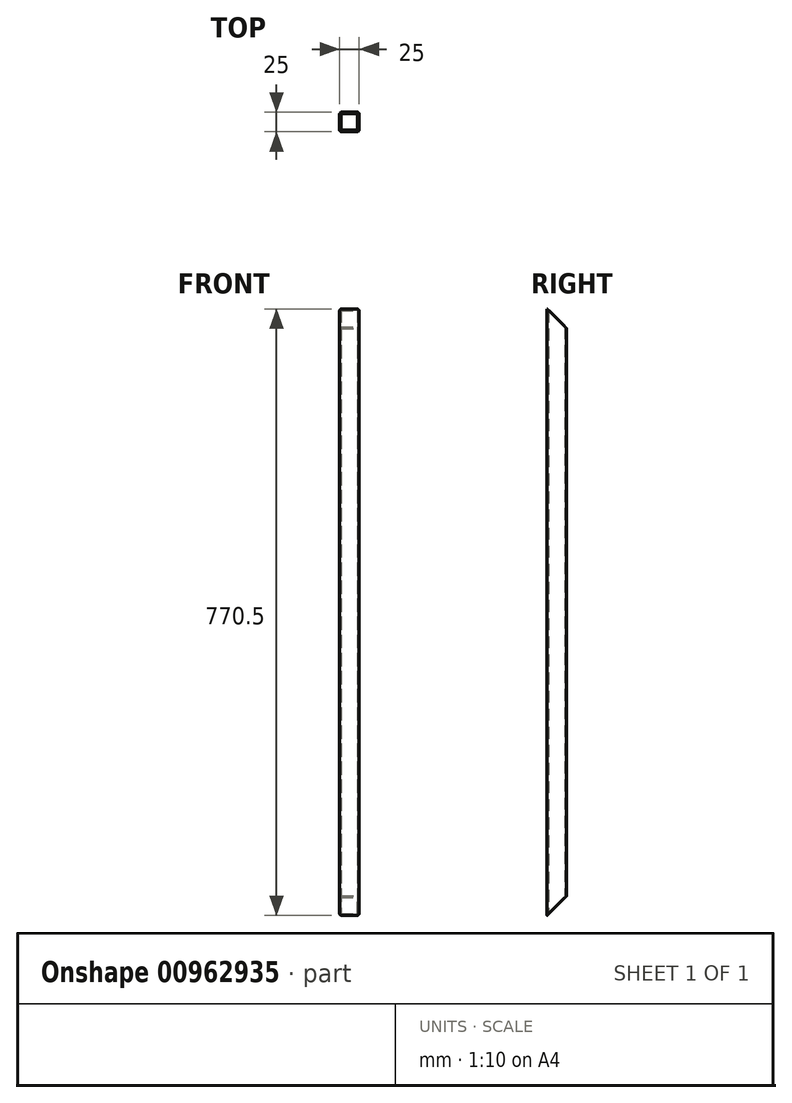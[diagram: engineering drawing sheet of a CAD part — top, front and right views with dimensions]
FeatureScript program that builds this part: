
annotation { "Feature Type Name" : "Feature", "Feature Type Description" : "" }
export const myFeature = defineFeature(function(context is Context, id is Id, definition is map)
    precondition{}
    {
        {
            var Q0;
            Q0=qCreatedBy(makeId("Top.planeOp"),FACE);
            var sketch = newSketch(context, id + "F0", { "sketchPlane" : qUnion([Q0])});
            skLineSegment(sketch, "E0.bottom", {"start": v(9.5, 12.5) * mm, "end": v(-9.5, 12.5) * mm});
            skLineSegment(sketch, "E0.top", {"start": v(9.5, -12.5) * mm, "end": v(-9.5, -12.5) * mm});
            skLineSegment(sketch, "E0.left", {"start": v(12.5, 9.5) * mm, "end": v(12.5, -9.5) * mm});
            skLineSegment(sketch, "E0.right", {"start": v(-12.5, 9.5) * mm, "end": v(-12.5, -9.5) * mm});
            skPoint(sketch, "E0.middle", {"position": v(0, 0) * mm});
            skPoint(sketch, "E1.visualSharp", {"position": v(-12.5, 12.5) * mm});
            skArc(sketch, "E1.filletArc", {"start": v(-9.5, 12.5) * mm, "mid": v(-11.62, 11.62) * mm, "end": v(-12.5, 9.5) * mm});
            skPoint(sketch, "E2.visualSharp", {"position": v(-12.5, -12.5) * mm});
            skArc(sketch, "E2.filletArc", {"start": v(-12.5, -9.5) * mm, "mid": v(-11.62, -11.62) * mm, "end": v(-9.5, -12.5) * mm});
            skPoint(sketch, "E3.visualSharp", {"position": v(12.5, -12.5) * mm});
            skArc(sketch, "E3.filletArc", {"start": v(9.5, -12.5) * mm, "mid": v(11.62, -11.62) * mm, "end": v(12.5, -9.5) * mm});
            skPoint(sketch, "E4.visualSharp", {"position": v(12.5, 12.5) * mm});
            skArc(sketch, "E4.filletArc", {"start": v(12.5, 9.5) * mm, "mid": v(11.62, 11.62) * mm, "end": v(9.5, 12.5) * mm});
            skLineSegment(sketch, "E5.0", {"start": v(10.5, 10.5) * mm, "end": v(-10.5, 10.5) * mm});
            skLineSegment(sketch, "E5.1", {"start": v(10.5, 10.5) * mm, "end": v(10.5, -10.5) * mm});
            skLineSegment(sketch, "E5.2", {"start": v(10.5, -10.5) * mm, "end": v(-10.5, -10.5) * mm});
            skLineSegment(sketch, "E5.3", {"start": v(-10.5, 10.5) * mm, "end": v(-10.5, -10.5) * mm});
            skSolve(sketch);
        }
        {
            var Q0;
            Q0=makeQuery(id+"F0.imprint","IMPRINT",FACE,{"disambiguationData":[TD([[makeQuery(id+"F0.imprint","IMPRINT",EDGE,{"derivedFrom":sQuery(id+"F0.wireOp",EDGE,"E0.bottom")}),1.0]])]});
            extrude(context, id + "F1", {"entities" : qUnion([Q0]), "depth" : 800 * mm, "offsetDistance" : 25 * mm});
        }
        {
            var Q0;
            Q0=qCreatedBy(makeId("Right.planeOp"),FACE);
            var sketch = newSketch(context, id + "F2", { "sketchPlane" : qUnion([Q0])});
            skLineSegment(sketch, "E6", {"start": v(-12.5, 0) * mm, "end": v(12.5, 25) * mm});
            skLineSegment(sketch, "E7", {"start": v(12.5, 25) * mm, "end": v(12.5, 0) * mm});
            skLineSegment(sketch, "E8", {"start": v(12.5, 0) * mm, "end": v(-12.5, 0) * mm});
            skLineSegment(sketch, "E9", {"start": v(12.5, 745.5) * mm, "end": v(12.5, 800) * mm});
            skLineSegment(sketch, "E10", {"start": v(12.5, 800) * mm, "end": v(-12.5, 800) * mm});
            skLineSegment(sketch, "E11", {"start": v(-12.5, 800) * mm, "end": v(-12.5, 770.5) * mm});
            skLineSegment(sketch, "E12", {"start": v(-12.5, 770.5) * mm, "end": v(12.5, 745.5) * mm});
            skSolve(sketch);
        }
        {
            var Q0;
            Q0 = qSketchRegion(id + "F2", true);
            extrude(context, id + "F3", {"entities" : qUnion([Q0]), "operationType" : NewBodyOperationType.REMOVE, "endBound" : BoundingType.SYMMETRIC, "oppositeDirection" : true, "depth" : 25 * mm, "offsetDistance" : 25 * mm});
        }
    });
